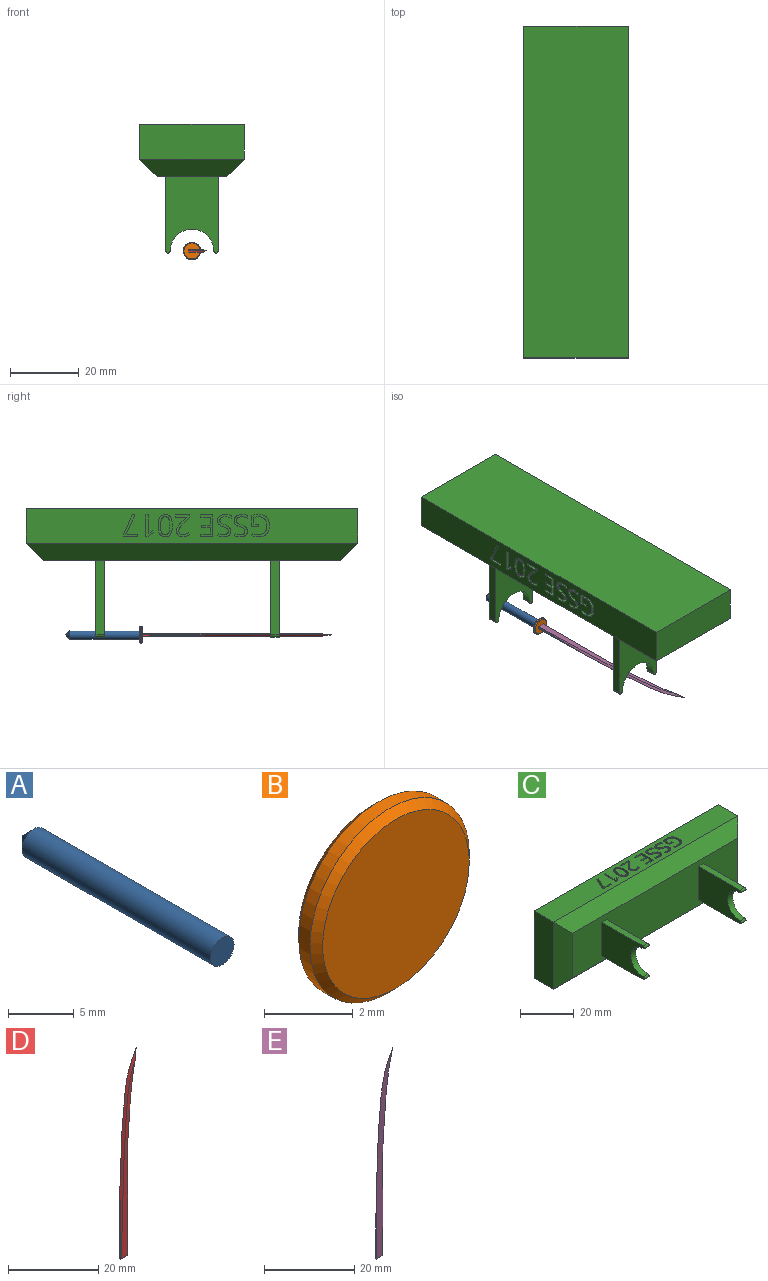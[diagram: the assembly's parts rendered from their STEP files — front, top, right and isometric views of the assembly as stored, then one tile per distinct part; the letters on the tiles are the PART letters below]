
ASSEMBLY  parts=5 mates=4
PART A: 3 faces, bbox 2.5x21.6x2.5 mm
  f0: cylinder r=1.27mm len=20.32mm, axis (0,1,0), area 162.1mm2, adj f1,f2
  f1: plane 2.54x2.54mm, normal (0,-1,0), area 5.1mm2, adj f0
  f2: cone r=0mm half-angle=45deg, axis (0,-1,0), area 7.2mm2, adj f0
PART B: 5 faces, bbox 5.1x0.8x5.1 mm
  f0: cylinder r=2.54mm len=5.08mm, axis (0,1,0), area 5.7mm2, adj f3,f4
  f1: plane 4.67x4.67mm, normal (0,-1,0), area 17.2mm2, adj f4
  f2: plane 4.67x4.67mm, normal (0,1,0), area 17.2mm2, adj f3
  f3: cone r=2.54mm half-angle=45deg, axis (0,-1,0), area 4.4mm2, adj f0,f2
  f4: cone r=2.34mm half-angle=45deg, axis (0,1,0), area 4.4mm2, adj f0,f1
PART C: 167 faces, bbox 96.5x37.5x30.5 mm
  f0: plane 96.52x10.16mm, normal (0,0,1), area 896.7mm2, adj f3,f4,f5,f8,f24,f25,f26,f27
  f1: plane 86.36x20.32mm, normal (0,-1,0), area 1677.4mm2, adj f6,f7,f8,f9,f12,f13,f15,f16
  f2: plane 96.52x10.16mm, normal (0,0,-1), area 980.6mm2, adj f3,f4,f5,f7
  f3: plane 30.48x10.16mm, normal (1,0,0), area 309.7mm2, adj f0,f2,f5,f9
  f4: plane 30.48x10.16mm, normal (-1,0,0), area 309.7mm2, adj f0,f2,f5,f6
  f5: plane 96.52x30.48mm, normal (0,1,0), area 2941.9mm2, adj f0,f2,f3,f4
  f6: plane 30.48x5.08mm, normal (-0.71,-0.71,0), area 182.5mm2, adj f1,f4,f7,f8
  f7: plane 96.52x5.08mm, normal (0,-0.71,-0.71), area 656.9mm2, adj f1,f2,f6,f9
  f8: plane 96.52x5.08mm, normal (0,-0.71,0.71), area 656.9mm2, adj f0,f1,f6,f9
  f9: plane 30.48x5.08mm, normal (0.71,-0.71,0), area 182.5mm2, adj f1,f3,f7,f8
  f10: cylinder r=6.35mm len=12.7mm, axis (1,0,0), area 50.7mm2, adj f11,f14,f15,f16
  f11: cylinder r=0.64mm len=2.54mm, axis (1,0,0), area 5.1mm2, adj f10,f12,f15,f16
  f12: plane 21.59x2.54mm, normal (0,0,-1), area 54.8mm2, adj f1,f11,f15,f16
  f13: plane 21.59x2.54mm, normal (0,0,1), area 54.8mm2, adj f1,f14,f15,f16
  f14: cylinder r=0.64mm len=2.54mm, axis (1,0,0), area 5.1mm2, adj f10,f13,f15,f16
  f15: plane 22.23x15.24mm, normal (-1,0,0), area 267mm2, adj f1,f10,f11,f12,f13,f14
  f16: plane 22.23x15.24mm, normal (1,0,0), area 267mm2, adj f1,f10,f11,f12,f13,f14
  f17: cylinder r=6.35mm len=12.7mm, axis (-1,0,0), area 50.7mm2, adj f18,f21,f22,f23
  f18: cylinder r=0.64mm len=2.54mm, axis (-1,0,0), area 5.1mm2, adj f17,f19,f22,f23
  f19: plane 21.59x2.54mm, normal (0,0,1), area 54.8mm2, adj f1,f18,f22,f23
  f20: plane 21.59x2.54mm, normal (0,0,-1), area 54.8mm2, adj f1,f21,f22,f23
  f21: cylinder r=0.64mm len=2.54mm, axis (-1,0,0), area 5.1mm2, adj f17,f20,f22,f23
  f22: plane 22.23x15.24mm, normal (1,0,0), area 267mm2, adj f1,f17,f18,f19,f20,f21
  f23: plane 22.23x15.24mm, normal (-1,0,0), area 267mm2, adj f1,f17,f18,f19,f20,f21
  f24: extruded ~2.54x2.41mm, area 6.3mm2, adj f0,f25,f39,f40
  f25: extruded ~2.54x1.56mm, area 4.7mm2, adj f0,f24,f26,f40
  f26: extruded ~2.54x1.56mm, area 4.7mm2, adj f0,f25,f27,f40
  f27: extruded ~2.54x2.44mm, area 6.4mm2, adj f0,f26,f28,f40
  f28: extruded ~2.54x2.42mm, area 6.4mm2, adj f0,f27,f29,f40
  f29: extruded ~2.54x1.55mm, area 4.7mm2, adj f0,f28,f30,f40
  f30: extruded ~2.54x1.57mm, area 4.7mm2, adj f0,f29,f39,f40
  f31: extruded ~2.54x2mm, area 5.2mm2, adj f32,f38,f40,f41
  f32: extruded ~2.54x1.03mm, area 3.2mm2, adj f31,f33,f40,f41
  f33: extruded ~2.54x1.04mm, area 3.3mm2, adj f32,f34,f40,f41
  f34: extruded ~2.54x1.99mm, area 5.2mm2, adj f33,f35,f40,f41
  f35: extruded ~2.54x1.99mm, area 5.2mm2, adj f34,f36,f40,f41
  f36: extruded ~2.54x1.04mm, area 3.3mm2, adj f35,f37,f40,f41
  f37: extruded ~2.54x1.03mm, area 3.2mm2, adj f36,f38,f40,f41
  f38: extruded ~2.54x2mm, area 5.2mm2, adj f31,f37,f40,f41
  f39: extruded ~2.54x2.44mm, area 6.4mm2, adj f0,f24,f30,f40
  f40: plane 6.48x4.16mm, normal (0,0,1), area 10.5mm2, adj f24,f25,f26,f27,f28,f29,f30,f31
  f41: plane 5.25x2.71mm, normal (0,0,1), area 12mm2, adj f31,f32,f33,f34,f35,f36,f37,f38
  f42: plane 2.54x0.79mm, normal (0,-1,0), area 2mm2, adj f0,f43,f48,f49
  f43: plane 5.72x2.57mm, normal (0.91,-0.41,0), area 15.9mm2, adj f0,f42,f44,f49
  f44: plane 2.54x0.57mm, normal (1,0,0), area 1.5mm2, adj f0,f43,f45,f49
  f45: plane 4.19x2.54mm, normal (0,1,0), area 10.6mm2, adj f0,f44,f46,f49
  f46: plane 2.54x0.66mm, normal (-1,0,0), area 1.7mm2, adj f0,f45,f47,f49
  f47: plane 3.43x2.54mm, normal (0,-1,0), area 8.7mm2, adj f0,f46,f48,f49
  f48: plane 5.64x2.61mm, normal (-0.91,0.42,0), area 15.8mm2, adj f0,f42,f47,f49
  f49: plane 6.3x4.19mm, normal (0,0,1), area 7mm2, adj f42,f43,f44,f45,f46,f47,f48
  f50: plane 6.3x2.54mm, normal (1,0,0), area 16mm2, adj f0,f51,f58,f59
  f51: plane 2.54x0.6mm, normal (0,1,0), area 1.5mm2, adj f0,f50,f52,f59
  f52: plane 2.54x1.67mm, normal (-0.61,0.79,0), area 5.3mm2, adj f0,f51,f53,f59
  f53: plane 2.54x0.49mm, normal (-0.79,-0.61,0), area 1.6mm2, adj f0,f52,f54,f59
  f54: extruded ~2.54x1.02mm, area 3.4mm2, adj f0,f53,f55,f59
  f55: extruded ~2.54x0.2mm, area 0.7mm2, adj f0,f54,f56,f59
  f56: extruded ~2.54x1.06mm, area 2.7mm2, adj f0,f55,f57,f59
  f57: plane 4.49x2.54mm, normal (-1,0,0), area 11.4mm2, adj f0,f56,f58,f59
  f58: plane 2.54x0.7mm, normal (0,-1,0), area 1.8mm2, adj f0,f50,f57,f59
  f59: plane 6.3x2.27mm, normal (0,0,1), area 5.4mm2, adj f50,f51,f52,f53,f54,f55,f56,f57
  f60: plane 2.54x0.66mm, normal (1,0,0), area 1.7mm2, adj f0,f61,f79,f80
  f61: plane 3.24x2.54mm, normal (0,1,0), area 8.2mm2, adj f0,f60,f62,f80
  f62: plane 2.54x0.03mm, normal (1,0,0), area 0.1mm2, adj f0,f61,f63,f80
  f63: plane 2.54x1.38mm, normal (0.7,-0.71,0), area 4.9mm2, adj f0,f62,f64,f80
  f64: extruded ~2.54x1.48mm, area 4.9mm2, adj f0,f63,f65,f80
  f65: extruded ~2.54x1.19mm, area 3.2mm2, adj f0,f64,f66,f80
  f66: extruded ~2.54x1.22mm, area 3.5mm2, adj f0,f65,f67,f80
  f67: extruded ~2.54x1.39mm, area 3.8mm2, adj f0,f66,f68,f80
  f68: extruded ~2.54x1.9mm, area 5.3mm2, adj f0,f67,f69,f80
  f69: plane 2.54x0.49mm, normal (-0.79,-0.61,0), area 1.6mm2, adj f0,f68,f70,f80
  f70: extruded ~2.54x0.78mm, area 2.3mm2, adj f0,f69,f71,f80
  f71: extruded ~2.54x0.74mm, area 1.9mm2, adj f0,f70,f72,f80
  f72: extruded ~2.54x0.85mm, area 2.3mm2, adj f0,f71,f73,f80
  f73: extruded ~2.54x0.8mm, area 2.2mm2, adj f0,f72,f74,f80
  f74: extruded ~2.54x0.67mm, area 1.7mm2, adj f0,f73,f75,f80
  f75: extruded ~2.54x0.64mm, area 1.9mm2, adj f0,f74,f76,f80
  f76: extruded ~2.54x1.1mm, area 3.8mm2, adj f0,f75,f77,f80
  f77: plane 2.54x1.67mm, normal (-0.71,0.71,0), area 6mm2, adj f0,f76,f78,f80
  f78: plane 2.54x0.62mm, normal (-1,0,0), area 1.6mm2, adj f0,f77,f79,f80
  f79: plane 4.14x2.54mm, normal (0,-1,0), area 10.5mm2, adj f0,f60,f78,f80
  f80: plane 6.39x4.14mm, normal (0,0,1), area 8.7mm2, adj f60,f61,f62,f63,f64,f65,f66,f67
  f81: plane 2.54x0.65mm, normal (1,0,0), area 1.7mm2, adj f0,f82,f92,f93
  f82: plane 2.78x2.54mm, normal (0,1,0), area 7.1mm2, adj f0,f81,f83,f93
  f83: plane 2.54x2.32mm, normal (1,0,0), area 5.9mm2, adj f0,f82,f84,f93
  f84: plane 2.61x2.54mm, normal (0,-1,0), area 6.6mm2, adj f0,f83,f85,f93
  f85: plane 2.54x0.65mm, normal (1,0,0), area 1.6mm2, adj f0,f84,f86,f93
  f86: plane 2.61x2.54mm, normal (0,1,0), area 6.6mm2, adj f0,f85,f87,f93
  f87: plane 2.54x2.03mm, normal (1,0,0), area 5.2mm2, adj f0,f86,f88,f93
  f88: plane 2.78x2.54mm, normal (0,-1,0), area 7.1mm2, adj f0,f87,f89,f93
  f89: plane 2.54x0.65mm, normal (1,0,0), area 1.7mm2, adj f0,f88,f90,f93
  f90: plane 3.51x2.54mm, normal (0,1,0), area 8.9mm2, adj f0,f89,f91,f93
  f91: plane 6.3x2.54mm, normal (-1,0,0), area 16mm2, adj f0,f90,f92,f93
  f92: plane 3.51x2.54mm, normal (0,-1,0), area 8.9mm2, adj f0,f81,f91,f93
  f93: plane 6.3x3.51mm, normal (0,0,1), area 9.9mm2, adj f81,f82,f83,f84,f85,f86,f87,f88
  f94: extruded ~2.54x1.05mm, area 2.9mm2, adj f0,f95,f118,f119
  f95: extruded ~2.54x1.36mm, area 4mm2, adj f0,f94,f96,f119
  f96: extruded ~2.54x0.88mm, area 2.4mm2, adj f0,f95,f97,f119
  f97: extruded ~2.54x0.41mm, area 1.4mm2, adj f0,f96,f98,f119
  f98: extruded ~2.54x0.54mm, area 1.4mm2, adj f0,f97,f99,f119
  f99: extruded ~2.54x0.69mm, area 2mm2, adj f0,f98,f100,f119
  f100: extruded ~2.54x0.91mm, area 2.4mm2, adj f0,f99,f101,f119
  f101: extruded ~2.54x1.52mm, area 4mm2, adj f0,f100,f102,f119
  f102: plane 2.54x0.64mm, normal (0.94,-0.34,0), area 1.7mm2, adj f0,f101,f103,f119
  f103: extruded ~2.54x1.73mm, area 4.5mm2, adj f0,f102,f104,f119
  f104: extruded ~2.54x1.45mm, area 3.9mm2, adj f0,f103,f105,f119
  f105: extruded ~2.54x1.16mm, area 3.4mm2, adj f0,f104,f106,f119
  f106: extruded ~2.54x1.12mm, area 3.1mm2, adj f0,f105,f107,f119
  f107: extruded ~2.54x1.25mm, area 3.7mm2, adj f0,f106,f108,f119
  f108: extruded ~2.54x0.94mm, area 2.6mm2, adj f0,f107,f109,f119
  f109: extruded ~2.54x0.44mm, area 1.5mm2, adj f0,f108,f110,f119
  f110: extruded ~2.54x0.54mm, area 1.4mm2, adj f0,f109,f111,f119
  f111: extruded ~2.54x0.77mm, area 2.3mm2, adj f0,f110,f112,f119
  f112: extruded ~2.54x1.1mm, area 2.9mm2, adj f0,f111,f113,f119
  f113: extruded ~2.54x0.9mm, area 2.3mm2, adj f0,f112,f114,f119
  f114: extruded ~2.54x0.84mm, area 2.2mm2, adj f0,f113,f115,f119
  f115: plane 2.54x0.71mm, normal (-1,0,0), area 1.8mm2, adj f0,f114,f116,f119
  f116: extruded ~2.54x1.72mm, area 4.5mm2, adj f0,f115,f117,f119
  f117: extruded ~2.54x1.64mm, area 4.4mm2, adj f0,f116,f118,f119
  f118: extruded ~2.54x1.3mm, area 3.8mm2, adj f0,f94,f117,f119
  f119: plane 6.47x3.96mm, normal (0,0,1), area 9.2mm2, adj f94,f95,f96,f97,f98,f99,f100,f101
  f120: extruded ~2.54x1.05mm, area 2.9mm2, adj f0,f121,f144,f145
  f121: extruded ~2.54x1.36mm, area 4mm2, adj f0,f120,f122,f145
  f122: extruded ~2.54x0.88mm, area 2.4mm2, adj f0,f121,f123,f145
  f123: extruded ~2.54x0.41mm, area 1.4mm2, adj f0,f122,f124,f145
  f124: extruded ~2.54x0.54mm, area 1.4mm2, adj f0,f123,f125,f145
  f125: extruded ~2.54x0.69mm, area 2mm2, adj f0,f124,f126,f145
  f126: extruded ~2.54x0.91mm, area 2.4mm2, adj f0,f125,f127,f145
  f127: extruded ~2.54x1.52mm, area 4mm2, adj f0,f126,f128,f145
  f128: plane 2.54x0.64mm, normal (0.94,-0.34,0), area 1.7mm2, adj f0,f127,f129,f145
  f129: extruded ~2.54x1.73mm, area 4.5mm2, adj f0,f128,f130,f145
  f130: extruded ~2.54x1.45mm, area 3.9mm2, adj f0,f129,f131,f145
  f131: extruded ~2.54x1.16mm, area 3.4mm2, adj f0,f130,f132,f145
  f132: extruded ~2.54x1.12mm, area 3.1mm2, adj f0,f131,f133,f145
  f133: extruded ~2.54x1.25mm, area 3.7mm2, adj f0,f132,f134,f145
  f134: extruded ~2.54x0.94mm, area 2.6mm2, adj f0,f133,f135,f145
  f135: extruded ~2.54x0.44mm, area 1.5mm2, adj f0,f134,f136,f145
  f136: extruded ~2.54x0.54mm, area 1.4mm2, adj f0,f135,f137,f145
  f137: extruded ~2.54x0.77mm, area 2.3mm2, adj f0,f136,f138,f145
  f138: extruded ~2.54x1.1mm, area 2.9mm2, adj f0,f137,f139,f145
  f139: extruded ~2.54x0.9mm, area 2.3mm2, adj f0,f138,f140,f145
  f140: extruded ~2.54x0.84mm, area 2.2mm2, adj f0,f139,f141,f145
  f141: plane 2.54x0.71mm, normal (-1,0,0), area 1.8mm2, adj f0,f140,f142,f145
  f142: extruded ~2.54x1.72mm, area 4.5mm2, adj f0,f141,f143,f145
  f143: extruded ~2.54x1.64mm, area 4.4mm2, adj f0,f142,f144,f145
  f144: extruded ~2.54x1.3mm, area 3.8mm2, adj f0,f120,f143,f145
  f145: plane 6.47x3.96mm, normal (0,0,1), area 9.2mm2, adj f120,f121,f122,f123,f124,f125,f126,f127
  f146: plane 2.54x0.65mm, normal (-1,0,0), area 1.7mm2, adj f0,f147,f165,f166
  f147: plane 2.54x1.41mm, normal (0,-1,0), area 3.6mm2, adj f0,f146,f148,f166
  f148: plane 2.54x1.94mm, normal (-1,0,0), area 4.9mm2, adj f0,f147,f149,f166
  f149: extruded ~2.54x1.28mm, area 3.3mm2, adj f0,f148,f150,f166
  f150: extruded ~2.54x1.83mm, area 5.1mm2, adj f0,f149,f151,f166
  f151: extruded ~2.54x1.93mm, area 5.3mm2, adj f0,f150,f152,f166
  f152: extruded ~2.54x1.9mm, area 5.2mm2, adj f0,f151,f153,f166
  f153: extruded ~2.54x1.8mm, area 5mm2, adj f0,f152,f154,f166
  f154: extruded ~2.54x1.64mm, area 4.3mm2, adj f0,f153,f155,f166
  f155: plane 2.54x0.65mm, normal (0.92,-0.4,0), area 1.8mm2, adj f0,f154,f156,f166
  f156: extruded ~2.54x1.88mm, area 4.9mm2, adj f0,f155,f157,f166
  f157: extruded ~2.54x1.73mm, area 4.6mm2, adj f0,f156,f158,f166
  f158: extruded ~2.54x1.14mm, area 4.1mm2, adj f0,f157,f159,f166
  f159: extruded ~2.54x1.72mm, area 4.5mm2, adj f0,f158,f160,f166
  f160: extruded ~2.54x2.38mm, area 6.5mm2, adj f0,f159,f161,f166
  f161: extruded ~2.54x2.23mm, area 6.2mm2, adj f0,f160,f162,f166
  f162: extruded ~2.54x1.2mm, area 3.1mm2, adj f0,f161,f163,f166
  f163: extruded ~2.54x1.02mm, area 2.7mm2, adj f0,f162,f164,f166
  f164: plane 3.06x2.54mm, normal (1,0,0), area 7.8mm2, adj f0,f163,f165,f166
  f165: plane 2.54x2.14mm, normal (0,1,0), area 5.4mm2, adj f0,f146,f164,f166
  f166: plane 6.47x5.24mm, normal (0,0,1), area 12mm2, adj f146,f147,f148,f149,f150,f151,f152,f153
PART D: 7 faces, bbox 7x0.5x58.7 mm
  f0: plane 18.58x0.34mm, normal (-1,0,0), area 3.1mm2, adj f1,f5,f6
  f1: plane 2.03x0.38mm, normal (0,0,-1), area 0.8mm2, adj f0,f2,f4,f5,f6
  f2: plane 17.78x0.38mm, normal (1,0,0), area 6.8mm2, adj f1,f3,f4,f5
  f3: extruded ~37.14x3.17mm, area 13.6mm2, adj f2,f4,f5,f6
  f4: plane 52x4.41mm, normal (0,-1,0), area 61.4mm2, adj f1,f2,f3,f6
  f5: plane 55.02x5.22mm, normal (0,1,0), area 91.9mm2, adj f0,f1,f2,f3,f6
  f6: bspline ~58.69x7.03mm, area 35mm2, adj f0,f1,f3,f4,f5
PART E: 7 faces, bbox 7x0.5x58.7 mm
  f0: plane 18.58x0.34mm, normal (-1,0,0), area 3.1mm2, adj f1,f4,f6
  f1: plane 2.03x0.38mm, normal (0,0,-1), area 0.8mm2, adj f0,f2,f4,f5,f6
  f2: plane 17.78x0.38mm, normal (1,0,0), area 6.8mm2, adj f1,f3,f4,f5
  f3: extruded ~37.14x3.17mm, area 13.6mm2, adj f2,f4,f5,f6
  f4: plane 55.02x5.22mm, normal (0,-1,0), area 91.9mm2, adj f0,f1,f2,f3,f6
  f5: plane 52x4.41mm, normal (0,1,0), area 61.4mm2, adj f1,f2,f3,f6
  f6: bspline ~58.69x7.04mm, area 35mm2, adj f0,f1,f3,f4,f5
PLACE A t=(-6.57,2.87,-1.05)mm
PLACE B t=(-6.57,2.87,-1.05)mm
PLACE C rot(axis=(0.58,-0.58,-0.58),120deg) t=(-6.57,-32.69,35.78)mm
PLACE D rot(axis=(1,0,0),90deg) t=(-7.59,-18.21,-1.05)mm
PLACE E rot(axis=(1,0,0),90deg) t=(-7.59,-18.21,-0.67)mm
MATE fastened D.f5 <-> E.f4  axis (0,0,1) through (-5.55,-27.1,-1.05)mm
MATE fastened A.f0 <-> C.f17  axis (0,1,0) through (-6.57,-7.29,-1.05)mm
MATE fastened E.f1 <-> B.f0  axis (0,1,0) through (-6.57,-18.21,-1.05)mm
MATE fastened B.f0 <-> A.f0  axis (0,1,0) through (-6.57,-17.45,-1.05)mm
